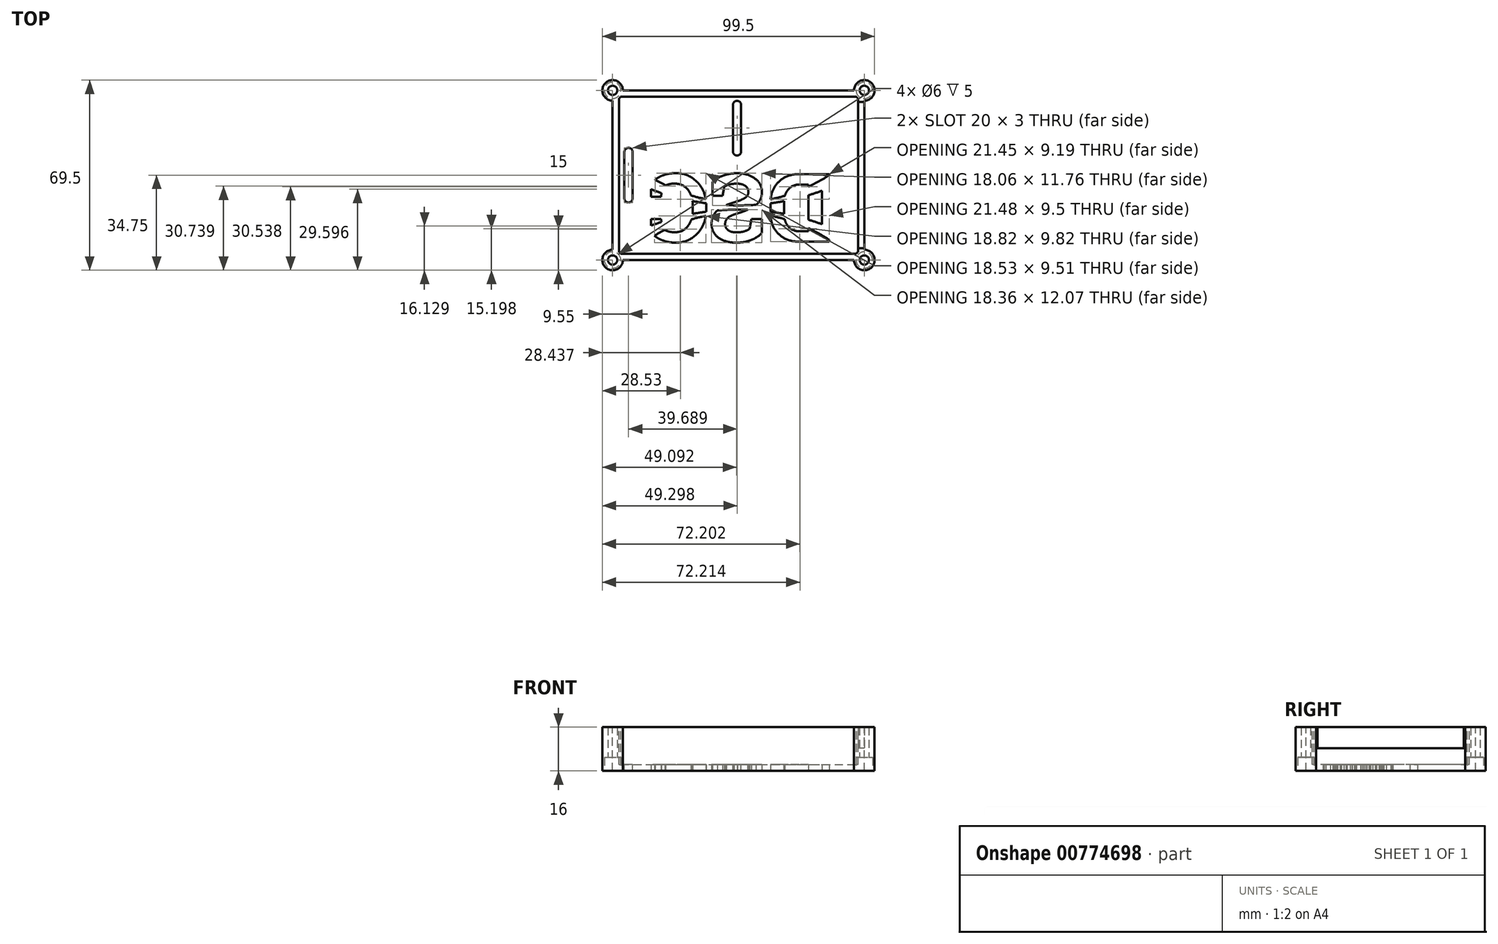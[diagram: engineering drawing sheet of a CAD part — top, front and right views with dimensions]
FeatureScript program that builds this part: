
annotation { "Feature Type Name" : "Feature", "Feature Type Description" : "" }
export const myFeature = defineFeature(function(context is Context, id is Id, definition is map)
    precondition{}
    {
        {
            var Q0;
            Q0=qCreatedBy(makeId("Top.planeOp"),FACE);
            var sketch = newSketch(context, id + "F0", { "sketchPlane" : qUnion([Q0])});
            skLineSegment(sketch, "E0.bottom", {"start": v(-46, 31) * mm, "end": v(46, 31) * mm});
            skLineSegment(sketch, "E0.top", {"start": v(-46, -31) * mm, "end": v(46, -31) * mm});
            skLineSegment(sketch, "E0.left", {"start": v(-46, 31) * mm, "end": v(-46, -31) * mm});
            skLineSegment(sketch, "E0.right", {"start": v(46, 31) * mm, "end": v(46, -31) * mm});
            skSolve(sketch);
        }
        {
            var Q0;
            Q0 = qSketchRegion(id + "F0", true);
            extrude(context, id + "F1", {"entities" : qUnion([Q0]), "depth" : 16 * mm, "offsetDistance" : 25 * mm});
        }
        {
            var Q0;
            Q0=makeQuery(id+"F1.opExtrude","CAP_FACE",FACE,{"disambiguationData":[OSD([sQuery(id+"F0.wireOp",EDGE,"E0.bottom"),sQuery(id+"F0.wireOp",EDGE,"E0.top"),sQuery(id+"F0.wireOp",EDGE,"E0.left"),sQuery(id+"F0.wireOp",EDGE,"E0.right")])],"isStart":false});
            shell(context, id + "F2", {"entities" : qUnion([Q0]), "thickness" : 2.3 * mm});
        }
        {
            var Q0;
            Q0=makeQuery(id+"F2.opShell","OFFSET_FACE",FACE,{"disambiguationData":[OSD([sQuery(id+"F0.wireOp",EDGE,"E0.bottom"),sQuery(id+"F0.wireOp",EDGE,"E0.top"),sQuery(id+"F0.wireOp",EDGE,"E0.left"),sQuery(id+"F0.wireOp",EDGE,"E0.right")])]});
            var sketch = newSketch(context, id + "F3", { "sketchPlane" : qUnion([Q0])});
            skLineSegment(sketch, "E1.bottom", {"start": v(49.32, 26.75) * mm, "end": v(39.32, 26.75) * mm});
            skLineSegment(sketch, "E1.top", {"start": v(49.32, -26.75) * mm, "end": v(39.32, -26.75) * mm});
            skLineSegment(sketch, "E1.left", {"start": v(49.32, 26.75) * mm, "end": v(49.32, -26.75) * mm});
            skLineSegment(sketch, "E1.right", {"start": v(39.32, 26.75) * mm, "end": v(39.32, -26.75) * mm});
            skSolve(sketch);
        }
        {
            var Q0;
            Q0 = qSketchRegion(id + "F3", true);
            extrude(context, id + "F4", {"entities" : qUnion([Q0]), "operationType" : NewBodyOperationType.REMOVE, "depth" : 25 * mm, "offsetDistance" : 25 * mm, "hasSecondDirection" : true, "secondDirectionOppositeDirection" : false, "secondDirectionDepth" : 6 * mm});
        }
        {
            var Q0;
            Q0=makeQuery(id+"F2.opShell","OFFSET_FACE",FACE,{"disambiguationData":[OSD([sQuery(id+"F0.wireOp",EDGE,"E0.bottom"),sQuery(id+"F0.wireOp",EDGE,"E0.top"),sQuery(id+"F0.wireOp",EDGE,"E0.left"),sQuery(id+"F0.wireOp",EDGE,"E0.right")])]});
            var sketch = newSketch(context, id + "F5", { "sketchPlane" : qUnion([Q0])});
            skLineSegment(sketch, "E2.left", {"start": v(-2.01, 25.7) * mm, "end": v(-2.01, 8.7) * mm});
            skLineSegment(sketch, "E2.right", {"start": v(0.99, 25.7) * mm, "end": v(0.99, 8.7) * mm});
            skArc(sketch, "E3", {"start": v(0.99, 25.7) * mm, "mid": v(-0.51, 27.2) * mm, "end": v(-2.01, 25.7) * mm});
            skArc(sketch, "E4", {"start": v(-2.01, 8.7) * mm, "mid": v(-0.51, 7.2) * mm, "end": v(0.99, 8.7) * mm});
            skLineSegment(sketch, "E5.left", {"start": v(-41.7, 8.5) * mm, "end": v(-41.7, -8.5) * mm});
            skLineSegment(sketch, "E5.right", {"start": v(-38.7, 8.5) * mm, "end": v(-38.7, -8.5) * mm});
            skArc(sketch, "E6", {"start": v(-38.7, 8.5) * mm, "mid": v(-40.2, 10) * mm, "end": v(-41.7, 8.5) * mm});
            skArc(sketch, "E7", {"start": v(-41.7, -8.5) * mm, "mid": v(-40.2, -10) * mm, "end": v(-38.7, -8.5) * mm});
            skSolve(sketch);
        }
        {
            var Q0;
            Q0 = qSketchRegion(id + "F5", true);
            extrude(context, id + "F6", {"entities" : qUnion([Q0]), "operationType" : NewBodyOperationType.REMOVE, "oppositeDirection" : true, "depth" : 5 * mm, "offsetDistance" : 25 * mm});
        }
        {
            var Q0;
            {var subQ0=sQuery(id+"F0.wireOp",EDGE,"E0.top");Q0=makeQuery(id+"F68QWxwM45a5B5R_1.boolean.opBoolean","MERGE",FACE,{"derivedFrom":[makeQuery(id+"F1.opExtrude","CAP_FACE",FACE,{"disambiguationData":[OSD([sQuery(id+"F0.wireOp",EDGE,"E0.bottom"),subQ0,sQuery(id+"F0.wireOp",EDGE,"E0.left"),sQuery(id+"F0.wireOp",EDGE,"E0.right")])],"isStart":true}),makeQuery(id+"F68QWxwM45a5B5R_1.opExtrude","CAP_FACE",FACE,{"disambiguationData":[OSD([subQ0,sQuery(id+"F74UQLEKdTQEZdR_1.wireOp",EDGE,"755a6f8e-ed04-46e4-b94c-7a49e4ab0227"),sQuery(id+"F74UQLEKdTQEZdR_1.wireOp",EDGE,"02a90ea7-267a-43d1-a396-4d7aca61ef3c"),sQuery(id+"F74UQLEKdTQEZdR_1.wireOp",EDGE,"ebf3dd87-de29-4995-9c31-cb9386e9db1e")])],"isStart":false})]});}
            var sketch = newSketch(context, id + "F7", { "sketchPlane" : qUnion([Q0])});
            skText(sketch, "E8", { "text": "DSC", "fontName": "RobotoSlab-Bold.ttf"});
            skArc(sketch, "E9", {"start": v(34.14, -0.7) * mm, "mid": v(0, 9.97) * mm, "end": v(-34.14, -0.7) * mm});
            skArc(sketch, "E10", {"start": v(-34.14, 24.3) * mm, "mid": v(0, 13.65) * mm, "end": v(34.14, 24.3) * mm});
            skArc(sketch, "E11", {"start": v(34.14, 4.3) * mm, "mid": v(0, 11.03) * mm, "end": v(-34.14, 4.3) * mm});
            skArc(sketch, "E12", {"start": v(-34.14, 19.3) * mm, "mid": v(0, 12.58) * mm, "end": v(34.14, 19.3) * mm});
            const initialGuessF7  = {"E8": [0.03414, 0.0243, -1, 0, 0.025]};
            skSetInitialGuess(sketch, initialGuessF7);
            skSolve(sketch);
        }
        {
            var Q0;
            {var subQ5=sQuery(id+"F7.wireOp",EDGE,"E8.sketch_text.stroke-0");Q0=makeQuery(id+"F7.imprint","IMPRINT",FACE,{"disambiguationData":[TD([[makeQuery(id+"F7.imprint","IMPRINT",EDGE,{"derivedFrom":subQ5}),-1.0]])]});}
            var Q1;
            {var subQ1=sQuery(id+"F7.wireOp",EDGE,"E8.sketch_text.stroke-17");Q1=makeQuery(id+"F7.imprint","IMPRINT",FACE,{"disambiguationData":[TD([[makeQuery(id+"F7.imprint","IMPRINT",EDGE,{"derivedFrom":subQ1}),-1.0]])]});}
            var Q2;
            {var subQ8=sQuery(id+"F7.wireOp",EDGE,"E8.sketch_text.stroke-4");Q2=makeQuery(id+"F7.imprint","IMPRINT",FACE,{"disambiguationData":[TD([[makeQuery(id+"F7.imprint","IMPRINT",EDGE,{"derivedFrom":subQ8}),-1.0]])]});}
            var Q3;
            {var subQ0=sQuery(id+"F7.wireOp",EDGE,"E12");var subQ1=sQuery(id+"F7.wireOp",EDGE,"E8.sketch_text.stroke-8");var subQ2=makeQuery(id+"F7.imprint","INTERSECT",VERTEX,{"derivedFrom":[subQ1,subQ0]});Q3=makeQuery(id+"F7.imprint","IMPRINT",FACE,{"disambiguationData":[TD([[makeQuery(id+"F7.imprint","IMPRINT",EDGE,{"disambiguationData":[TD([[subQ2,-1.0]])],"derivedFrom":subQ1}),-1.0]])]});}
            var Q4;
            Q4=makeQuery(id+"F7.imprint","IMPRINT",FACE,{"disambiguationData":[TD([[makeQuery(id+"F7.imprint","IMPRINT",EDGE,{"derivedFrom":sQuery(id+"F7.wireOp",EDGE,"E8.sketch_text.stroke-21")}),-1.0]])]});
            var Q5;
            {var subQ0=sQuery(id+"F7.wireOp",EDGE,"E9");var subQ1=sQuery(id+"F7.wireOp",EDGE,"E8.sketch_text.stroke-29");var subQ2=makeQuery(id+"F7.imprint","INTERSECT",VERTEX,{"derivedFrom":[subQ1,subQ0]});Q5=makeQuery(id+"F7.imprint","IMPRINT",FACE,{"disambiguationData":[TD([[makeQuery(id+"F7.imprint","IMPRINT",EDGE,{"disambiguationData":[TD([[subQ2,-1.0]])],"derivedFrom":subQ1}),-1.0]])]});}
            var Q6;
            {var subQ5=sQuery(id+"F7.wireOp",EDGE,"E8.sketch_text.stroke-30");var subQ6=sQuery(id+"F7.wireOp",EDGE,"E8.sketch_text.stroke-29");var subQ7=makeQuery(id+"F7.imprint","INTERSECT",VERTEX,{"derivedFrom":[subQ6,subQ5]});Q6=makeQuery(id+"F7.imprint","IMPRINT",FACE,{"disambiguationData":[TD([[makeQuery(id+"F7.imprint","IMPRINT",EDGE,{"disambiguationData":[TD([[subQ7,1.0]])],"derivedFrom":subQ6}),-1.0]])]});}
            var Q7;
            {var subQ5=sQuery(id+"F7.wireOp",EDGE,"E8.sketch_text.stroke-31");Q7=makeQuery(id+"F7.imprint","IMPRINT",FACE,{"disambiguationData":[TD([[makeQuery(id+"F7.imprint","IMPRINT",EDGE,{"derivedFrom":subQ5}),-1.0]])]});}
            var Q8;
            {var subQ4=sQuery(id+"F7.wireOp",EDGE,"E8.sketch_text.stroke-54");Q8=makeQuery(id+"F7.imprint","IMPRINT",FACE,{"disambiguationData":[TD([[makeQuery(id+"F7.imprint","IMPRINT",EDGE,{"derivedFrom":subQ4}),-1.0]])]});}
            var Q9;
            {var subQ1=sQuery(id+"F7.wireOp",EDGE,"E8.sketch_text.stroke-57");Q9=makeQuery(id+"F7.imprint","IMPRINT",FACE,{"disambiguationData":[TD([[makeQuery(id+"F7.imprint","IMPRINT",EDGE,{"derivedFrom":subQ1}),-1.0]])]});}
            var Q10;
            {var subQ9=sQuery(id+"F7.wireOp",EDGE,"E8.sketch_text.stroke-59");Q10=makeQuery(id+"F7.imprint","IMPRINT",FACE,{"disambiguationData":[TD([[makeQuery(id+"F7.imprint","IMPRINT",EDGE,{"derivedFrom":subQ9}),-1.0]])]});}
            var Q11;
            {var subQ0=sQuery(id+"F7.wireOp",EDGE,"E8.sketch_text.stroke-63");Q11=makeQuery(id+"F7.imprint","IMPRINT",FACE,{"disambiguationData":[TD([[makeQuery(id+"F7.imprint","IMPRINT",EDGE,{"derivedFrom":subQ0}),-1.0]])]});}
            var Q12;
            {var subQ0=sQuery(id+"F7.wireOp",EDGE,"E8.sketch_text.stroke-51");Q12=makeQuery(id+"F7.imprint","IMPRINT",FACE,{"disambiguationData":[TD([[makeQuery(id+"F7.imprint","IMPRINT",EDGE,{"derivedFrom":subQ0}),-1.0]])]});}
            extrude(context, id + "F8", {"entities" : qUnion([Q0, Q1, Q2, Q3, Q4, Q5, Q6, Q7, Q8, Q9, Q10, Q11, Q12]), "operationType" : NewBodyOperationType.REMOVE, "oppositeDirection" : true, "depth" : 5 * mm, "offsetDistance" : 25 * mm});
        }
        {
            var Q0;
            {var subQ0=sQuery(id+"F0.wireOp",EDGE,"E0.top");Q0=makeQuery(id+"F68QWxwM45a5B5R_1.boolean.opBoolean","MERGE",FACE,{"derivedFrom":[makeQuery(id+"F1.opExtrude","CAP_FACE",FACE,{"disambiguationData":[OSD([sQuery(id+"F0.wireOp",EDGE,"E0.bottom"),subQ0,sQuery(id+"F0.wireOp",EDGE,"E0.left"),sQuery(id+"F0.wireOp",EDGE,"E0.right")])],"isStart":false}),makeQuery(id+"F68QWxwM45a5B5R_1.opExtrude","CAP_FACE",FACE,{"disambiguationData":[OSD([subQ0,sQuery(id+"F74UQLEKdTQEZdR_1.wireOp",EDGE,"755a6f8e-ed04-46e4-b94c-7a49e4ab0227"),sQuery(id+"F74UQLEKdTQEZdR_1.wireOp",EDGE,"02a90ea7-267a-43d1-a396-4d7aca61ef3c"),sQuery(id+"F74UQLEKdTQEZdR_1.wireOp",EDGE,"ebf3dd87-de29-4995-9c31-cb9386e9db1e")])],"isStart":true})]});}
            var sketch = newSketch(context, id + "F9", { "sketchPlane" : qUnion([Q0])});
            skCircle(sketch, "E13", {"center": v(-46, 31) * mm, "radius": 3.75 * mm});
            skCircle(sketch, "E14", {"center": v(46, 31) * mm, "radius": 3.75 * mm});
            skCircle(sketch, "E15", {"center": v(-46, -31) * mm, "radius": 3.75 * mm});
            skCircle(sketch, "E16", {"center": v(46, -31) * mm, "radius": 3.75 * mm});
            skSolve(sketch);
        }
        {
            var Q0;
            Q0 = qSketchRegion(id + "F9", true);
            extrude(context, id + "F10", {"entities" : qUnion([Q0]), "operationType" : NewBodyOperationType.ADD, "oppositeDirection" : true, "depth" : 16 * mm, "offsetDistance" : 25 * mm});
        }
        {
            var Q0;
            {var subQ0=sQuery(id+"F0.wireOp",EDGE,"E0.top");Q0=makeQuery(id+"F10.boolean.opBoolean","MERGE",FACE,{"derivedFrom":[makeQuery(id+"F68QWxwM45a5B5R_1.boolean.opBoolean","MERGE",FACE,{"derivedFrom":[makeQuery(id+"F1.opExtrude","CAP_FACE",FACE,{"disambiguationData":[OSD([sQuery(id+"F0.wireOp",EDGE,"E0.bottom"),subQ0,sQuery(id+"F0.wireOp",EDGE,"E0.left"),sQuery(id+"F0.wireOp",EDGE,"E0.right")])],"isStart":true}),makeQuery(id+"F68QWxwM45a5B5R_1.opExtrude","CAP_FACE",FACE,{"disambiguationData":[OSD([subQ0,sQuery(id+"F74UQLEKdTQEZdR_1.wireOp",EDGE,"755a6f8e-ed04-46e4-b94c-7a49e4ab0227"),sQuery(id+"F74UQLEKdTQEZdR_1.wireOp",EDGE,"02a90ea7-267a-43d1-a396-4d7aca61ef3c"),sQuery(id+"F74UQLEKdTQEZdR_1.wireOp",EDGE,"ebf3dd87-de29-4995-9c31-cb9386e9db1e")])],"isStart":false})]}),makeQuery(id+"F10.opExtrude","CAP_FACE",FACE,{"disambiguationData":[OSD([sQuery(id+"F9.wireOp",EDGE,"E13")])],"isStart":false}),makeQuery(id+"F10.opExtrude","CAP_FACE",FACE,{"disambiguationData":[OSD([sQuery(id+"F9.wireOp",EDGE,"E14")])],"isStart":false}),makeQuery(id+"F10.opExtrude","CAP_FACE",FACE,{"disambiguationData":[OSD([sQuery(id+"F9.wireOp",EDGE,"E15")])],"isStart":false}),makeQuery(id+"F10.opExtrude","CAP_FACE",FACE,{"disambiguationData":[OSD([sQuery(id+"F9.wireOp",EDGE,"E16")])],"isStart":false})]});}
            var sketch = newSketch(context, id + "F11", { "sketchPlane" : qUnion([Q0])});
            skPoint(sketch, "E17", {"position": v(46, -31) * mm});
            skPoint(sketch, "E18", {"position": v(-46, -31) * mm});
            skPoint(sketch, "E19", {"position": v(-46, 31) * mm});
            skPoint(sketch, "E20", {"position": v(46, 31) * mm});
            skSolve(sketch);
        }
        {
            var Q0;
            Q0=sQuery(id+"F11.wireOp",VERTEX,"E17");
            var Q1;
            Q1=sQuery(id+"F11.wireOp",VERTEX,"E18");
            var Q2;
            Q2=sQuery(id+"F11.wireOp",VERTEX,"E19");
            var Q3;
            Q3=sQuery(id+"F11.wireOp",VERTEX,"E20");
            var Q4;
            Q4=makeQuery(id+"F1.opExtrude","SWEPT_BODY",BODY,{"disambiguationData":[OSD([sQuery(id+"F0.wireOp",EDGE,"E0.bottom"),sQuery(id+"F0.wireOp",EDGE,"E0.top"),sQuery(id+"F0.wireOp",EDGE,"E0.left"),sQuery(id+"F0.wireOp",EDGE,"E0.right")])]});
            hole(context, id + "F12", {"style" : HoleStyle.C_BORE, "endStyle" : HoleEndStyle.THROUGH, "holeDiameter" : 3.4 * mm, "cBoreDiameter" : 6 * mm, "cBoreDepth" : 5 * mm, "majorDiameter" : 5 * mm, "isTappedThrough" : true, "tappedDepth" : 12 * mm, "tapClearance" : 3, "startFromSketch" : true, "locations" : qUnion([Q0, Q1, Q2, Q3]), "scope" : qUnion([Q4])});
        }
    });
